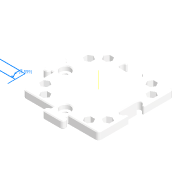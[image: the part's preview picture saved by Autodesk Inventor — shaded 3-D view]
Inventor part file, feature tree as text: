
AUTODESK INVENTOR PART (.ipt)
format: ipt  version: 2022 (Build 260153000, 153)  size: 608,768 bytes
history: native  units: mm
features: sketch x7, extrude x6, other x4, projected_geometry x3, mirror x2, reference x2, pattern_circular x1, hole x1, chamfer x1, fillet x1, plane x1
ambient origin geometry x8: Origin, YZ Plane, XZ Plane, XY Plane, X Axis, Y Axis, Z Axis, Center Point
bodies: Volumenkörper1 (feature_tree)
feature tree (29):
  extrude  "Extrusion1"  TaperAngle=0.0deg  [1 undecoded]
  mirror  "Mirror6"
  mirror  "Mirror7"
  extrude  "Extrusion13"  TaperAngle=0.0deg  [1 undecoded]
  extrude  "Extrusion14"  TaperAngle=0.0deg  [1 undecoded]
  other  "Work Axis4"
  pattern_circular  "Circular Pattern6"  [2 undecoded]
  hole  "Hole7"  [1 undecoded]
  chamfer  "Fase4"  Distance=3.0mm
  fillet  "Rundung5"  [1 undecoded]
  extrude  "Extrusion18"  TaperAngle=0.0deg  [1 undecoded]
  extrude  "Extrusion19"  TaperAngle=0.0deg  [1 undecoded]
  plane  "Arbeitsebene14"
  extrude  "Extrusion20"  TaperAngle=0.0deg  [1 undecoded]
  sketch  "Skizze1"  dims[d5=0.0mm d6=0.0mm]
  sketch  "Sketch26"  dims[d7=0.0mm d8=0.0mm]
  projected_geometry  "Projected Loop21"
  sketch  "Sketch28"  dims[d9=0.0mm d13=0.0mm]
  sketch  "Sketch29"  dims[d14=0.0mm]
  projected_geometry  "Projected Loop24"
  projected_geometry  "Projizierte Kontur27"
  sketch  "Skizze33"  dims[d20=0.0mm]
  sketch  "Skizze34"  dims[d21=0.0mm]
  reference  "Referenz9"
  sketch  "Skizze35"  dims[d22=0.0mm d23=0.0mm d24=0.0mm d25=3.0mm d26=0.0mm d27=0.0mm d28=0.0mm d29=0.0mm d30=0.0mm d31=0.0mm d32=0.0mm d33=0.0mm d34=0.0mm d46=0.0mm d47=0.0mm d48=0.0mm d49=-10.0mm d50=0.0mm d51=0.0mm d52=0.0mm d53=0.0mm d54=0.0mm d55=0.0mm d56=0.0mm d57=0.0mm d58=0.0mm d59=0.0mm d77=2.65mm d82=2.65mm d222=0.5mm d236=5.3mm d278=25.0mm d279=25.0mm d2=8.0mm d281=8.0mm d282=2.0mm d286=5.1mm d290=20.8mm d292=2.0mm d293=5.6mm d298=10.0mm d299=0.0mm d300=2.0mm d301=0.25mm d302=10.0mm d303=0.0mm d308=20.0mm d309=90.0deg d313=6.3mm d314=6.3mm d319=7.78mm d320=5.0mm d322=5.0mm d323=3.2mm d324=6.0mm d325=7.0mm d326=3.0mm d327=90.0deg d328=8.0mm d329=20.594885mm d331=0.0mm d332=0.0mm d360=0.5mm d361=2.0mm d362=45.0deg d365=7.0mm d367=7.0mm d369=4.2mm d370=0.0mm d380=45.0deg d384=0.75mm d385=5.0mm d386=5.0mm d387=2.0mm d388=0.25mm d391=0.1mm d392=5.05mm d393=5.05mm d394=1.96mm d396=5.45mm d397=7.05mm d398=10.0mm d399=0.0mm d401=10.0mm d402=0.0mm d403=0.1mm d404=3.558762mm d405=3.558762mm d406=5.0mm d407=15.0mm d408=0.0mm d409=0.0mm]
  reference  "Referenz10"
  other  "Assembly_Cassete_Deck.iam"
  other  "10_Base_puzzle_v3:3"
  other  "10_Cassete_Slide:1"
note: 10 required parameter values undecoded (feature->parameter linkage not recoverable at this tier; creation-order binding heuristic only, values carry confidence <= 0.55)
